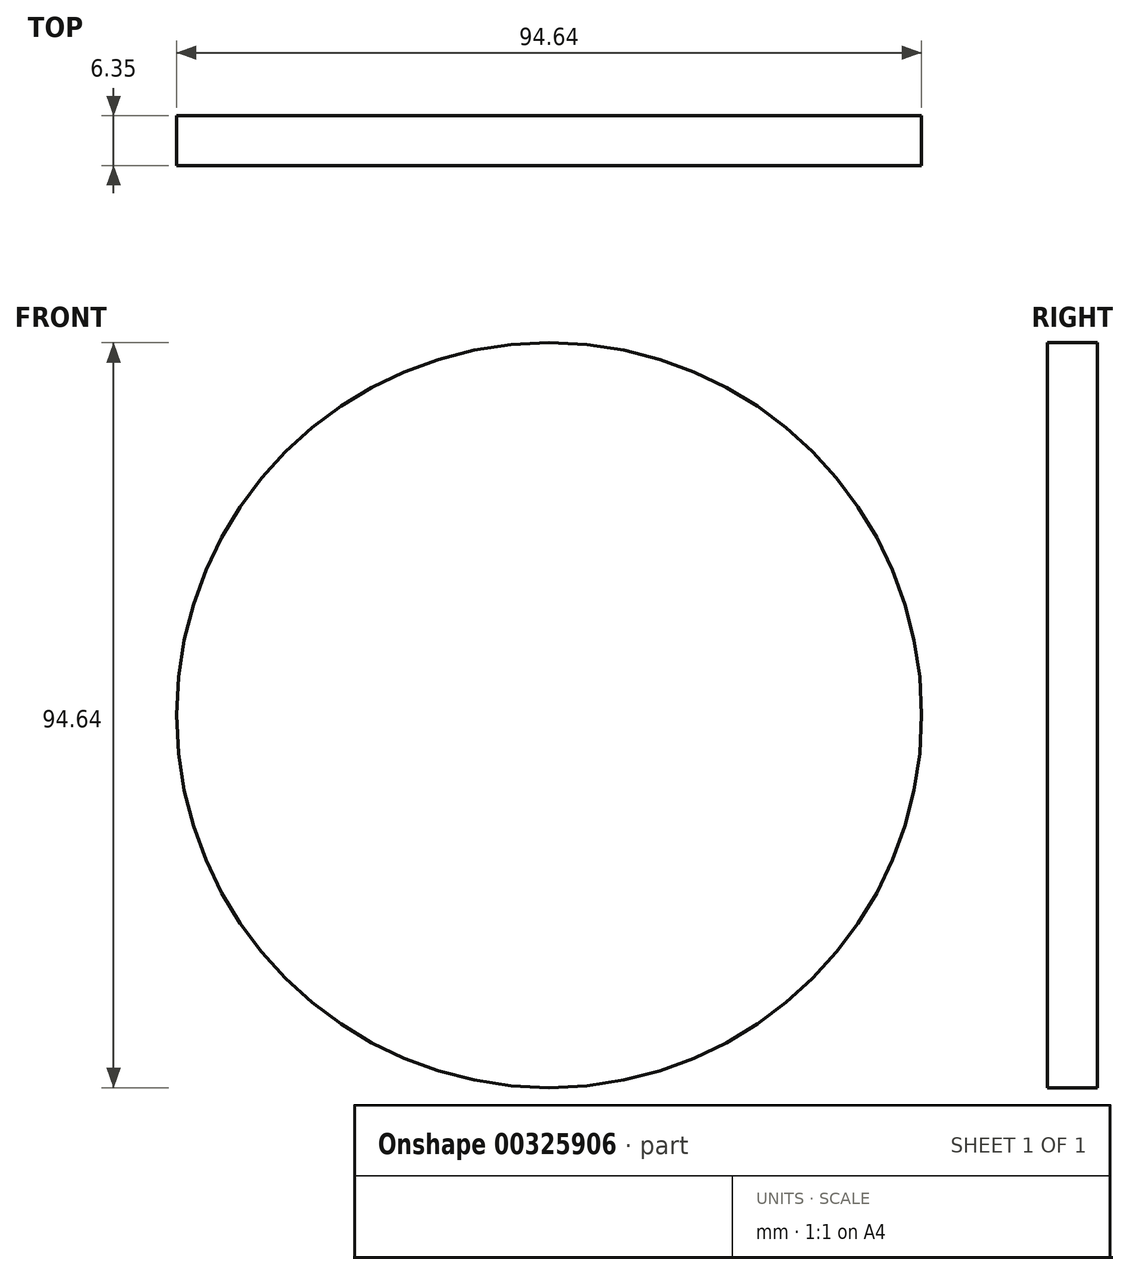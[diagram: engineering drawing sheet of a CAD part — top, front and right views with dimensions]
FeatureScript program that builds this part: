
annotation { "Feature Type Name" : "Feature", "Feature Type Description" : "" }
export const myFeature = defineFeature(function(context is Context, id is Id, definition is map)
    precondition{}
    {
        {
            var Q0;
            Q0=qCreatedBy(makeId("Front.planeOp"),FACE);
            var sketch = newSketch(context, id + "F0", { "sketchPlane" : qUnion([Q0])});
            skCircle(sketch, "E0", {"center": v(0, 0) * mm, "radius": 47.32 * mm});
            skSolve(sketch);
        }
        {
            var Q0;
            Q0=makeQuery(id+"F0.imprint","IMPRINT",FACE,{"disambiguationData":[TD([[makeQuery(id+"F0.imprint","IMPRINT",EDGE,{"derivedFrom":sQuery(id+"F0.wireOp",EDGE,"E0")}),1.0]])]});
            extrude(context, id + "F1", {"entities" : qUnion([Q0]), "depth" : 6.35 * mm});
        }
    });
